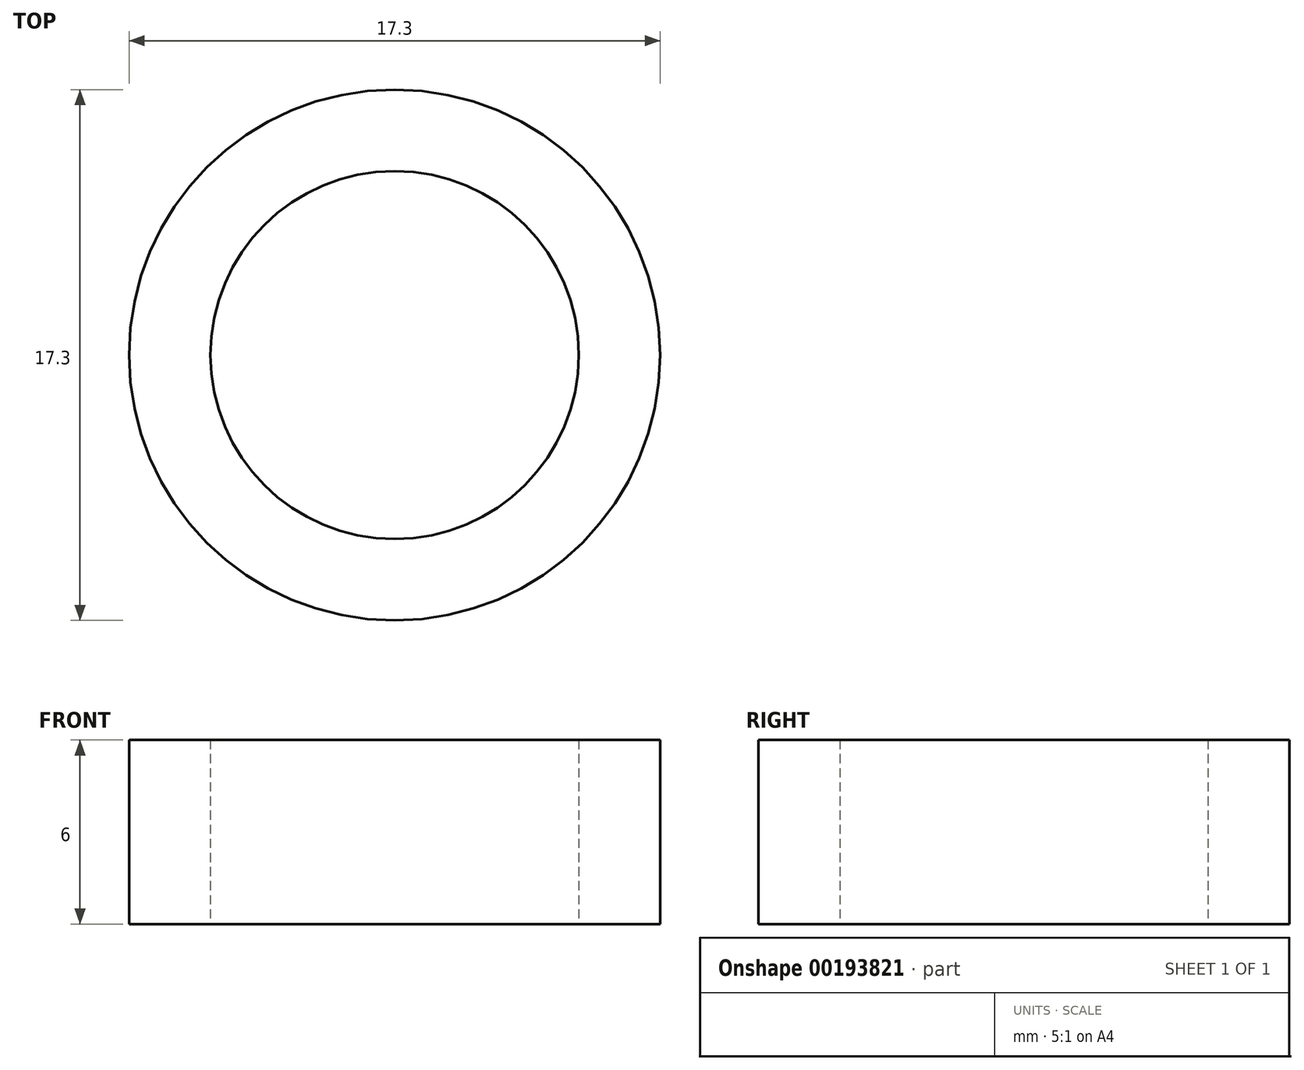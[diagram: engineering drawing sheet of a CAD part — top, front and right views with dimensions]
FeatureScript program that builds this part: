
annotation { "Feature Type Name" : "Feature", "Feature Type Description" : "" }
export const myFeature = defineFeature(function(context is Context, id is Id, definition is map)
    precondition{}
    {
        {
            var Q0;
            Q0=qCreatedBy(makeId("Top.planeOp"),FACE);
            var sketch = newSketch(context, id + "F0", { "sketchPlane" : qUnion([Q0])});
            skCircle(sketch, "E0", {"center": v(0, 0) * mm, "radius": 8.65 * mm});
            skCircle(sketch, "E1", {"center": v(0, 0) * mm, "radius": 6 * mm});
            skSolve(sketch);
        }
        {
            var Q0;
            Q0=makeQuery(id+"F0.imprint","IMPRINT",FACE,{"disambiguationData":[TD([[makeQuery(id+"F0.imprint","IMPRINT",EDGE,{"derivedFrom":sQuery(id+"F0.wireOp",EDGE,"E0")}),1.0]])]});
            extrude(context, id + "F1", {"entities" : qUnion([Q0]), "depth" : 6 * mm});
        }
    });
